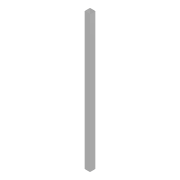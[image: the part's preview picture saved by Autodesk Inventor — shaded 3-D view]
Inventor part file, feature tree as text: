
AUTODESK INVENTOR PART (.ipt)
format: ipt  version: 2020.3 (Build 243373000, 373)  size: 89,600 bytes
history: native  units: mm
features: other x1, extrude x1, sketch x1
ambient origin geometry x8: Origin, YZ Plane, XZ Plane, XY Plane, X Axis, Y Axis, Z Axis, Center Point
bodies: Body1 (feature_tree)
feature tree (3):
  other  "Sólido1"
  extrude  "Extrusão1"  Depth=40.0mm
  sketch  "Esboço1"  dims[d0=40.0mm d1=40.0mm d2=1.5mm d3=1.5mm d4=1000.0mm d5=0.0mm]
